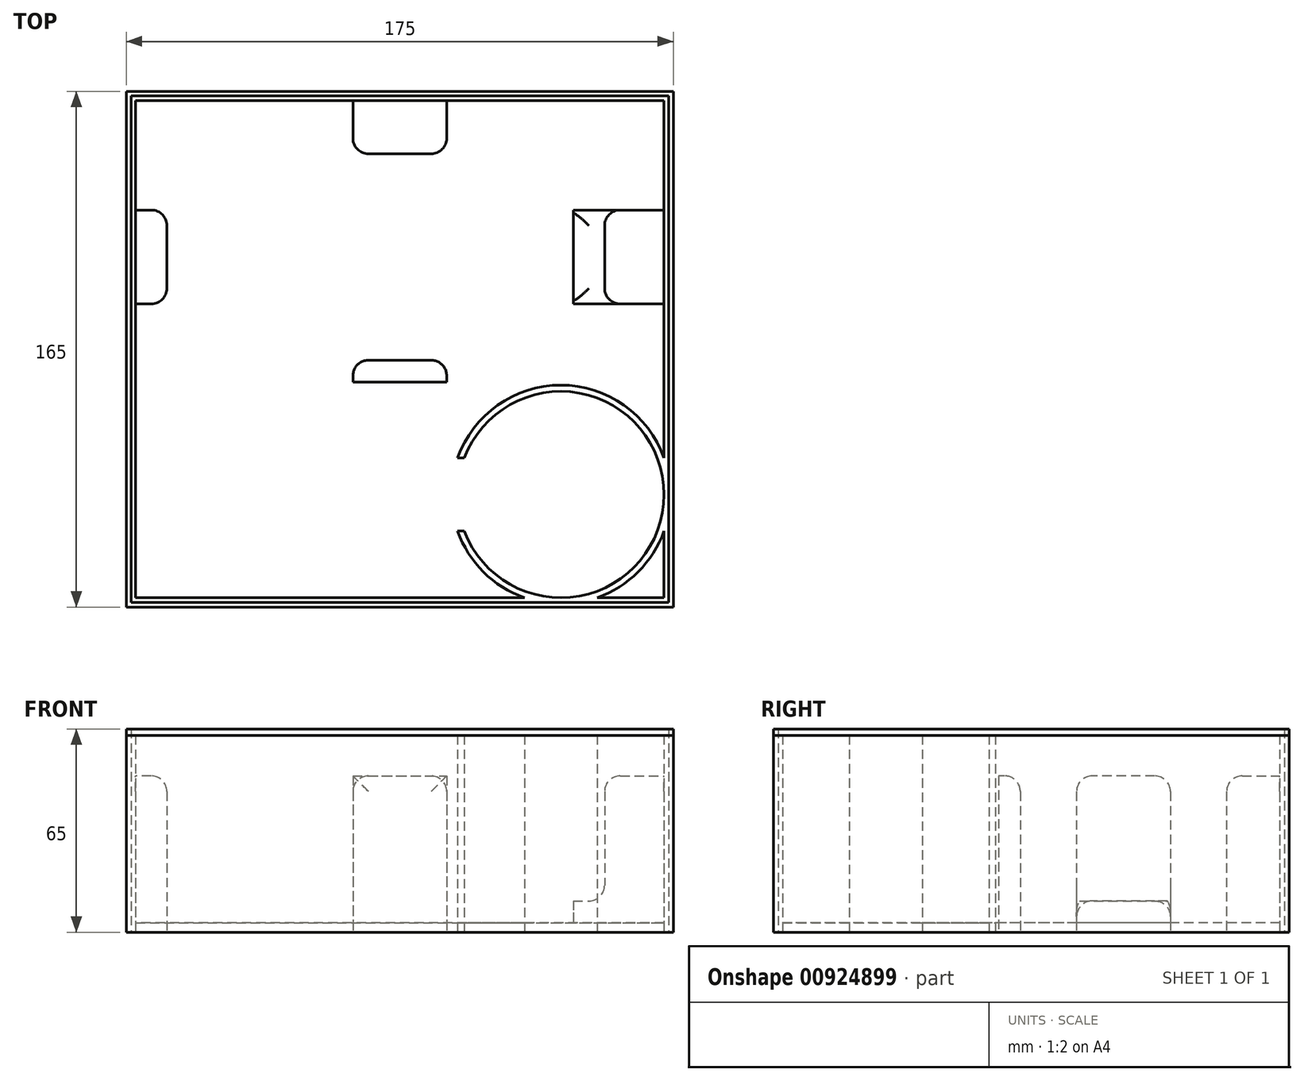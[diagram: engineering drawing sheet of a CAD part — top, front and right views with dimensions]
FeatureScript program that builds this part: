
annotation { "Feature Type Name" : "Feature", "Feature Type Description" : "" }
export const myFeature = defineFeature(function(context is Context, id is Id, definition is map)
    precondition{}
    {
        {
            var Q0;
            Q0=qCreatedBy(makeId("Top.planeOp"),FACE);
            var sketch = newSketch(context, id + "F0", { "sketchPlane" : qUnion([Q0])});
            skLineSegment(sketch, "E0.bottom", {"start": v(87.5, -82.5) * mm, "end": v(-87.5, -82.5) * mm});
            skLineSegment(sketch, "E0.top", {"start": v(87.5, 82.5) * mm, "end": v(-87.5, 82.5) * mm});
            skLineSegment(sketch, "E0.left", {"start": v(87.5, -82.5) * mm, "end": v(87.5, 82.5) * mm});
            skLineSegment(sketch, "E0.right", {"start": v(-87.5, -82.5) * mm, "end": v(-87.5, 82.5) * mm});
            skPoint(sketch, "E0.middle", {"position": v(0, 0) * mm});
            skLineSegment(sketch, "E1", {"start": v(-87.5, 82.5) * mm, "end": v(-84.5, 82.5) * mm, "construction": true});
            skLineSegment(sketch, "E2", {"start": v(-87.5, 82.5) * mm, "end": v(-87.5, 79.5) * mm, "construction": true});
            skLineSegment(sketch, "E3", {"start": v(-84.5, 79.5) * mm, "end": v(-84.5, -79.5) * mm});
            skLineSegment(sketch, "E4", {"start": v(-84.5, 79.5) * mm, "end": v(84.5, 79.5) * mm});
            skLineSegment(sketch, "E5", {"start": v(87.5, 82.5) * mm, "end": v(84.5, 82.5) * mm, "construction": true});
            skLineSegment(sketch, "E6", {"start": v(84.5, 79.5) * mm, "end": v(84.5, -34.84) * mm});
            skLineSegment(sketch, "E7", {"start": v(87.5, -82.5) * mm, "end": v(87.5, -79.5) * mm, "construction": true});
            skLineSegment(sketch, "E8", {"start": v(84.5, -79.5) * mm, "end": v(63.16, -79.5) * mm});
            skLineSegment(sketch, "E9", {"start": v(87.5, -82.5) * mm, "end": v(87.5, -46.5) * mm, "construction": true});
            skLineSegment(sketch, "E10", {"start": v(87.5, -46.5) * mm, "end": v(51.5, -46.5) * mm, "construction": true});
            skArc(sketch, "E11", {"start": v(20.63, -58.16) * mm, "mid": v(84.5, -46.5) * mm, "end": v(20.63, -34.84) * mm});
            skArc(sketch, "E12", {"start": v(63.16, -79.5) * mm, "mid": v(76.25, -71.25) * mm, "end": v(84.5, -58.16) * mm});
            skLineSegment(sketch, "E13.trimOffspring", {"start": v(39.84, -79.5) * mm, "end": v(-84.5, -79.5) * mm});
            skArc(sketch, "E14.trimOffspring", {"start": v(84.5, -34.84) * mm, "mid": v(51.5, -11.5) * mm, "end": v(18.5, -34.84) * mm});
            skLineSegment(sketch, "E15.trimOffspring", {"start": v(84.5, -58.16) * mm, "end": v(84.5, -79.5) * mm});
            skLineSegment(sketch, "E16", {"start": v(87.5, 82.5) * mm, "end": v(87.5, 29.5) * mm, "construction": true});
            skLineSegment(sketch, "E17", {"start": v(87.5, 29.5) * mm, "end": v(-87.5, 29.5) * mm, "construction": true});
            skLineSegment(sketch, "E18", {"start": v(-87.5, 29.5) * mm, "end": v(-74.5, 29.5) * mm, "construction": true});
            skLineSegment(sketch, "E19", {"start": v(87.5, 29.5) * mm, "end": v(65.5, 29.5) * mm, "construction": true});
            skLineSegment(sketch, "E20", {"start": v(65.5, 29.5) * mm, "end": v(65.5, 44.5) * mm});
            skLineSegment(sketch, "E21", {"start": v(65.5, 44.5) * mm, "end": v(84.5, 44.5) * mm});
            skLineSegment(sketch, "E22", {"start": v(65.5, 29.5) * mm, "end": v(65.5, 14.5) * mm});
            skLineSegment(sketch, "E23", {"start": v(65.5, 14.5) * mm, "end": v(84.5, 14.5) * mm});
            skLineSegment(sketch, "E24", {"start": v(65.5, 44.5) * mm, "end": v(55.5, 44.5) * mm});
            skLineSegment(sketch, "E25", {"start": v(65.5, 14.5) * mm, "end": v(55.5, 14.5) * mm});
            skLineSegment(sketch, "E26", {"start": v(55.5, 14.5) * mm, "end": v(55.5, 44.5) * mm});
            skLineSegment(sketch, "E27", {"start": v(-74.5, 29.5) * mm, "end": v(-74.5, 44.5) * mm});
            skLineSegment(sketch, "E28", {"start": v(-74.5, 44.5) * mm, "end": v(-84.5, 44.5) * mm});
            skLineSegment(sketch, "E29", {"start": v(-74.5, 29.5) * mm, "end": v(-74.5, 14.5) * mm});
            skLineSegment(sketch, "E30", {"start": v(-74.5, 14.5) * mm, "end": v(-84.5, 14.5) * mm});
            skLineSegment(sketch, "E31", {"start": v(87.5, 82.5) * mm, "end": v(0, 82.5) * mm});
            skLineSegment(sketch, "E32", {"start": v(87.5, 29.5) * mm, "end": v(0, 29.5) * mm, "construction": true});
            skLineSegment(sketch, "E33", {"start": v(0, 82.5) * mm, "end": v(0, 62.5) * mm, "construction": true});
            skLineSegment(sketch, "E34", {"start": v(0, 62.5) * mm, "end": v(-15, 62.5) * mm});
            skLineSegment(sketch, "E35", {"start": v(-15, 62.5) * mm, "end": v(-15, 79.5) * mm});
            skLineSegment(sketch, "E36", {"start": v(0, 62.5) * mm, "end": v(15, 62.5) * mm});
            skLineSegment(sketch, "E37", {"start": v(15, 62.5) * mm, "end": v(15, 79.5) * mm});
            skLineSegment(sketch, "E38", {"start": v(84.5, -34.84) * mm, "end": v(0, -34.84) * mm, "construction": true});
            skLineSegment(sketch, "E39", {"start": v(84.5, -58.16) * mm, "end": v(0, -58.16) * mm, "construction": true});
            skLineSegment(sketch, "E40", {"start": v(18.5, -34.84) * mm, "end": v(20.63, -34.84) * mm});
            skLineSegment(sketch, "E41", {"start": v(18.5, -58.16) * mm, "end": v(20.63, -58.16) * mm});
            skArc(sketch, "E42.trimOffspring", {"start": v(18.5, -58.16) * mm, "mid": v(26.75, -71.25) * mm, "end": v(39.84, -79.5) * mm});
            skLineSegment(sketch, "E43", {"start": v(0, 62.5) * mm, "end": v(0, -3.5) * mm, "construction": true});
            skLineSegment(sketch, "E44", {"start": v(0, -3.5) * mm, "end": v(-15, -3.5) * mm});
            skLineSegment(sketch, "E45", {"start": v(-15, -3.5) * mm, "end": v(-15, -10.5) * mm});
            skLineSegment(sketch, "E46", {"start": v(-15, -10.5) * mm, "end": v(15, -10.5) * mm});
            skLineSegment(sketch, "E47", {"start": v(15, -10.5) * mm, "end": v(15, -3.5) * mm});
            skLineSegment(sketch, "E48", {"start": v(15, -3.5) * mm, "end": v(0, -3.5) * mm});
            skLineSegment(sketch, "E49", {"start": v(-87.5, -82.5) * mm, "end": v(-86, -82.5) * mm, "construction": true});
            skLineSegment(sketch, "E50", {"start": v(-87.5, -82.5) * mm, "end": v(-87.5, -81) * mm, "construction": true});
            skLineSegment(sketch, "E51", {"start": v(87.5, 82.5) * mm, "end": v(87.5, 81) * mm, "construction": true});
            skLineSegment(sketch, "E52", {"start": v(87.5, -82.5) * mm, "end": v(86, -82.5) * mm, "construction": true});
            skLineSegment(sketch, "E53", {"start": v(-86, -81) * mm, "end": v(-86, 81) * mm});
            skLineSegment(sketch, "E54", {"start": v(86, -81) * mm, "end": v(86, 81) * mm});
            skLineSegment(sketch, "E55", {"start": v(87.5, -82.5) * mm, "end": v(87.5, -81) * mm});
            skLineSegment(sketch, "E56", {"start": v(86, -81) * mm, "end": v(-86, -81) * mm});
            skLineSegment(sketch, "E57", {"start": v(86, 81) * mm, "end": v(-86, 81) * mm});
            skPoint(sketch, "E58.orphan", {"position": v(-87.5, 81) * mm});
            skPoint(sketch, "E59.orphan", {"position": v(-86, 82.5) * mm});
            skPoint(sketch, "E60.orphan", {"position": v(86, 82.5) * mm});
            skSolve(sketch);
        }
        {
            var Q0;
            Q0=makeQuery(id+"F0.imprint","IMPRINT",FACE,{"disambiguationData":[TD([[makeQuery(id+"F0.imprint","IMPRINT",EDGE,{"derivedFrom":sQuery(id+"F0.wireOp",EDGE,"E0.bottom")}),-1.0]])]});
            var Q1;
            {var subQ1=sQuery(id+"F0.wireOp",EDGE,"E0.bottom");Q1=makeQuery(id+"F0.imprint","IMPRINT",FACE,{"disambiguationData":[TD([[makeQuery(id+"F0.imprint","IMPRINT",EDGE,{"derivedFrom":subQ1}),-1.0]])]});}
            var Q2;
            Q2=makeQuery(id+"F0.imprint","IMPRINT",FACE,{"disambiguationData":[TD([[makeQuery(id+"F0.imprint","IMPRINT",EDGE,{"derivedFrom":sQuery(id+"F0.wireOp",EDGE,"E8")}),1.0]])]});
            extrude(context, id + "F1", {"entities" : qUnion([Q0, Q1, Q2]), "depth" : 63 * mm, "offsetDistance" : 25 * mm});
        }
        {
            var Q0;
            Q0=makeQuery(id+"F0.imprint","IMPRINT",FACE,{"disambiguationData":[TD([[makeQuery(id+"F0.imprint","IMPRINT",EDGE,{"derivedFrom":sQuery(id+"F0.wireOp",EDGE,"E11")}),1.0]])]});
            var Q1;
            Q1=makeQuery(id+"F0.imprint","IMPRINT",FACE,{"disambiguationData":[TD([[makeQuery(id+"F0.imprint","IMPRINT",EDGE,{"derivedFrom":sQuery(id+"F0.wireOp",EDGE,"E27")}),1.0]])]});
            var Q2;
            Q2=makeQuery(id+"F0.imprint","IMPRINT",FACE,{"disambiguationData":[TD([[makeQuery(id+"F0.imprint","IMPRINT",EDGE,{"derivedFrom":sQuery(id+"F0.wireOp",EDGE,"E34")}),-1.0]])]});
            var Q3;
            Q3=makeQuery(id+"F0.imprint","IMPRINT",FACE,{"disambiguationData":[TD([[makeQuery(id+"F0.imprint","IMPRINT",EDGE,{"derivedFrom":sQuery(id+"F0.wireOp",EDGE,"E20")}),1.0]])]});
            var Q4;
            Q4=makeQuery(id+"F0.imprint","IMPRINT",FACE,{"disambiguationData":[TD([[makeQuery(id+"F0.imprint","IMPRINT",EDGE,{"derivedFrom":sQuery(id+"F0.wireOp",EDGE,"E20")}),-1.0]])]});
            var Q5;
            Q5=makeQuery(id+"F0.imprint","IMPRINT",FACE,{"disambiguationData":[TD([[makeQuery(id+"F0.imprint","IMPRINT",EDGE,{"derivedFrom":sQuery(id+"F0.wireOp",EDGE,"E44")}),1.0]])]});
            var Q6;
            Q6=makeQuery(id+"F0.imprint","IMPRINT",FACE,{"disambiguationData":[TD([[makeQuery(id+"F0.imprint","IMPRINT",EDGE,{"derivedFrom":sQuery(id+"F0.wireOp",EDGE,"E8")}),-1.0]])]});
            extrude(context, id + "F2", {"entities" : qUnion([Q0, Q1, Q2, Q3, Q4, Q5, Q6]), "depth" : 3 * mm, "offsetDistance" : 25 * mm});
        }
        {
            var Q0;
            Q0=makeQuery(id+"F0.imprint","IMPRINT",FACE,{"disambiguationData":[TD([[makeQuery(id+"F0.imprint","IMPRINT",EDGE,{"derivedFrom":sQuery(id+"F0.wireOp",EDGE,"E20")}),-1.0]])]});
            var Q1;
            Q1=makeQuery(id+"F0.imprint","IMPRINT",FACE,{"disambiguationData":[TD([[makeQuery(id+"F0.imprint","IMPRINT",EDGE,{"derivedFrom":sQuery(id+"F0.wireOp",EDGE,"E34")}),-1.0]])]});
            var Q2;
            Q2=makeQuery(id+"F0.imprint","IMPRINT",FACE,{"disambiguationData":[TD([[makeQuery(id+"F0.imprint","IMPRINT",EDGE,{"derivedFrom":sQuery(id+"F0.wireOp",EDGE,"E44")}),1.0]])]});
            var Q3;
            Q3=makeQuery(id+"F0.imprint","IMPRINT",FACE,{"disambiguationData":[TD([[makeQuery(id+"F0.imprint","IMPRINT",EDGE,{"derivedFrom":sQuery(id+"F0.wireOp",EDGE,"E27")}),1.0]])]});
            extrude(context, id + "F3", {"entities" : qUnion([Q0, Q1, Q2, Q3]), "depth" : 50 * mm, "offsetDistance" : 25 * mm});
        }
        {
            var Q0;
            Q0=makeQuery(id+"F0.imprint","IMPRINT",FACE,{"disambiguationData":[TD([[makeQuery(id+"F0.imprint","IMPRINT",EDGE,{"derivedFrom":sQuery(id+"F0.wireOp",EDGE,"E20")}),1.0]])]});
            extrude(context, id + "F4", {"entities" : qUnion([Q0]), "operationType" : NewBodyOperationType.ADD, "depth" : 10 * mm, "offsetDistance" : 25 * mm});
        }
        {
            var Q0;
            Q0=makeQuery(id+"F3.opExtrude","CAP_EDGE",EDGE,{"disambiguationData":[OSD([sQuery(id+"F0.wireOp",EDGE,"E30")])],"isStart":false});
            var Q1;
            Q1=makeQuery(id+"F3.opExtrude","CAP_EDGE",EDGE,{"disambiguationData":[OSD([sQuery(id+"F0.wireOp",EDGE,"E28")])],"isStart":false});
            var Q2;
            Q2=makeQuery(id+"F3.opExtrude","SWEPT_EDGE",EDGE,{"disambiguationData":[OSD([sQuery(id+"F0.wireOp",EDGE,"E27"),sQuery(id+"F0.wireOp",EDGE,"E28")])]});
            var Q3;
            Q3=makeQuery(id+"F3.opExtrude","SWEPT_EDGE",EDGE,{"disambiguationData":[OSD([sQuery(id+"F0.wireOp",EDGE,"E29"),sQuery(id+"F0.wireOp",EDGE,"E30")])]});
            var Q4;
            Q4=makeQuery(id+"F3.opExtrude","SWEPT_EDGE",EDGE,{"disambiguationData":[OSD([sQuery(id+"F0.wireOp",EDGE,"E22"),sQuery(id+"F0.wireOp",EDGE,"E23"),sQuery(id+"F0.wireOp",EDGE,"E25")])]});
            var Q5;
            Q5=makeQuery(id+"F3.opExtrude","SWEPT_FACE",FACE,{"disambiguationData":[OSD([sQuery(id+"F0.wireOp",EDGE,"E20"),sQuery(id+"F0.wireOp",EDGE,"E22")])]});
            var Q6;
            Q6=makeQuery(id+"F3.opExtrude","CAP_EDGE",EDGE,{"disambiguationData":[OSD([sQuery(id+"F0.wireOp",EDGE,"E23")])],"isStart":false});
            var Q7;
            Q7=makeQuery(id+"F3.opExtrude","CAP_EDGE",EDGE,{"disambiguationData":[OSD([sQuery(id+"F0.wireOp",EDGE,"E21")])],"isStart":false});
            var Q8;
            Q8=makeQuery(id+"F3.opExtrude","SWEPT_EDGE",EDGE,{"disambiguationData":[OSD([sQuery(id+"F0.wireOp",EDGE,"E36"),sQuery(id+"F0.wireOp",EDGE,"E37")])]});
            var Q9;
            Q9=makeQuery(id+"F3.opExtrude","SWEPT_EDGE",EDGE,{"disambiguationData":[OSD([sQuery(id+"F0.wireOp",EDGE,"E34"),sQuery(id+"F0.wireOp",EDGE,"E35")])]});
            var Q10;
            Q10=makeQuery(id+"F3.opExtrude","CAP_EDGE",EDGE,{"disambiguationData":[OSD([sQuery(id+"F0.wireOp",EDGE,"E34"),sQuery(id+"F0.wireOp",EDGE,"E36")])],"isStart":false});
            var Q11;
            Q11=makeQuery(id+"F3.opExtrude","CAP_EDGE",EDGE,{"disambiguationData":[OSD([sQuery(id+"F0.wireOp",EDGE,"E37")])],"isStart":false});
            var Q12;
            Q12=makeQuery(id+"F3.opExtrude","CAP_EDGE",EDGE,{"disambiguationData":[OSD([sQuery(id+"F0.wireOp",EDGE,"E35")])],"isStart":false});
            var Q13;
            Q13=makeQuery(id+"F3.opExtrude","CAP_EDGE",EDGE,{"disambiguationData":[OSD([sQuery(id+"F0.wireOp",EDGE,"E44"),sQuery(id+"F0.wireOp",EDGE,"E48")])],"isStart":false});
            var Q14;
            Q14=makeQuery(id+"F3.opExtrude","SWEPT_EDGE",EDGE,{"disambiguationData":[OSD([sQuery(id+"F0.wireOp",EDGE,"E44"),sQuery(id+"F0.wireOp",EDGE,"E45")])]});
            var Q15;
            Q15=makeQuery(id+"F3.opExtrude","SWEPT_EDGE",EDGE,{"disambiguationData":[OSD([sQuery(id+"F0.wireOp",EDGE,"E47"),sQuery(id+"F0.wireOp",EDGE,"E48")])]});
            var Q16;
            Q16=makeQuery(id+"F3.opExtrude","CAP_EDGE",EDGE,{"disambiguationData":[OSD([sQuery(id+"F0.wireOp",EDGE,"E27"),sQuery(id+"F0.wireOp",EDGE,"E29")])],"isStart":false});
            fillet(context, id + "F5", {"entities" : qUnion([Q0, Q1, Q2, Q3, Q4, Q5, Q6, Q7, Q8, Q9, Q10, Q11, Q12, Q13, Q14, Q15, Q16]), "radius" : 5 * mm, "tangentPropagation" : true, "allowEdgeOverflow" : false});
        }
        {
            var Q0;
            {var subQ1=sQuery(id+"F0.wireOp",EDGE,"E0.bottom");Q0=makeQuery(id+"F0.imprint","IMPRINT",FACE,{"disambiguationData":[TD([[makeQuery(id+"F0.imprint","IMPRINT",EDGE,{"derivedFrom":subQ1}),-1.0]])]});}
            extrude(context, id + "F6", {"entities" : qUnion([Q0]), "depth" : 65 * mm, "offsetDistance" : 25 * mm});
        }
    });
